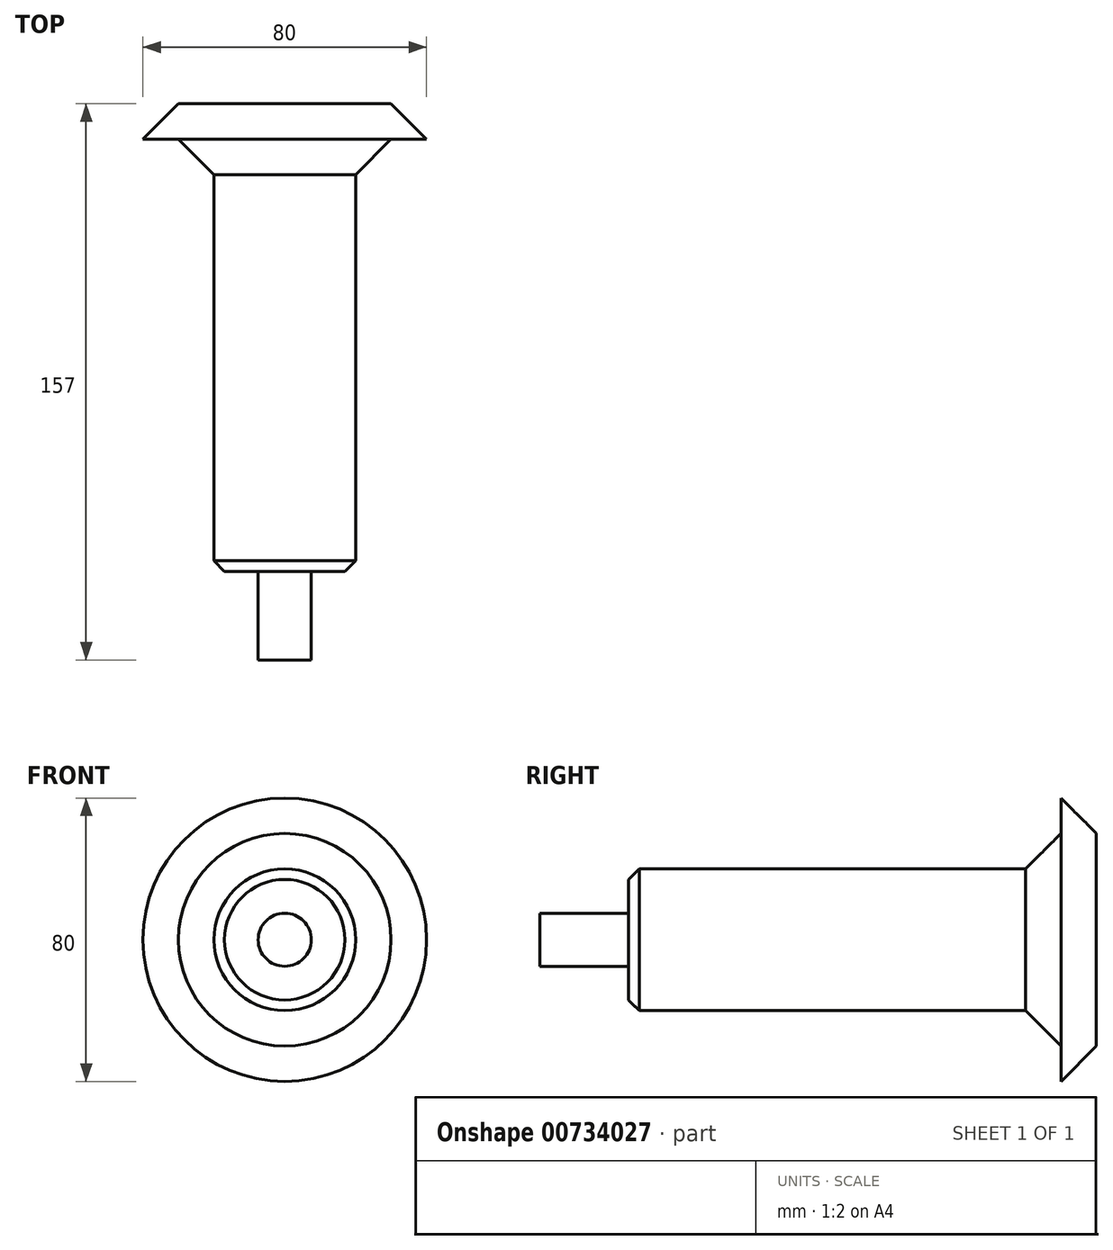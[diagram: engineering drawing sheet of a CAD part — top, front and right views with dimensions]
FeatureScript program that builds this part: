
annotation { "Feature Type Name" : "Feature", "Feature Type Description" : "" }
export const myFeature = defineFeature(function(context is Context, id is Id, definition is map)
    precondition{}
    {
        {
            var Q0;
            Q0=qCreatedBy(makeId("Front.planeOp"),FACE);
            var sketch = newSketch(context, id + "F0", { "sketchPlane" : qUnion([Q0])});
            skCircle(sketch, "E0", {"center": v(0, 0) * mm, "radius": 20 * mm});
            skSolve(sketch);
        }
        {
            var Q0;
            Q0 = qSketchRegion(id + "F0", true);
            extrude(context, id + "F1", {"entities" : qUnion([Q0]), "depth" : 112 * mm, "offsetDistance" : 25.4 * mm});
        }
        {
            var Q0;
            Q0=makeQuery(id+"F1.opExtrude","CAP_EDGE",EDGE,{"disambiguationData":[OSD([sQuery(id+"F0.wireOp",EDGE,"E0")])],"isStart":false});
            chamfer(context, id + "F2", {"entities" : qUnion([Q0]), "width" : 3 * mm, "tangentPropagation" : true});
        }
        {
            var Q0;
            Q0=makeQuery(id+"F1.opExtrude","CAP_FACE",FACE,{"disambiguationData":[OSD([sQuery(id+"F0.wireOp",EDGE,"E0")])],"isStart":false});
            var sketch = newSketch(context, id + "F3", { "sketchPlane" : qUnion([Q0])});
            skCircle(sketch, "E1", {"center": v(0, 0) * mm, "radius": 7.5 * mm});
            skSolve(sketch);
        }
        {
            var Q0;
            Q0 = qSketchRegion(id + "F3", true);
            extrude(context, id + "F4", {"entities" : qUnion([Q0]), "operationType" : NewBodyOperationType.ADD, "depth" : 25 * mm, "offsetDistance" : 25.4 * mm});
        }
        {
            var Q0;
            Q0=makeQuery(id+"F1.opExtrude","CAP_FACE",FACE,{"disambiguationData":[OSD([sQuery(id+"F0.wireOp",EDGE,"E0")])],"isStart":true});
            var sketch = newSketch(context, id + "F5", { "sketchPlane" : qUnion([Q0])});
            skCircle(sketch, "E2", {"center": v(0, 0) * mm, "radius": 30 * mm});
            skSolve(sketch);
        }
        {
            var Q0;
            Q0 = qSketchRegion(id + "F5", true);
            extrude(context, id + "F6", {"entities" : qUnion([Q0]), "operationType" : NewBodyOperationType.ADD, "depth" : 10 * mm, "offsetDistance" : 25.4 * mm});
        }
        {
            var Q0;
            Q0=makeQuery(id+"F6.opExtrude","CAP_EDGE",EDGE,{"disambiguationData":[OSD([sQuery(id+"F5.wireOp",EDGE,"E2")])],"isStart":true});
            chamfer(context, id + "F7", {"entities" : qUnion([Q0]), "width" : 10 * mm, "tangentPropagation" : true});
        }
        {
            var Q0;
            Q0=makeQuery(id+"F6.opExtrude","CAP_FACE",FACE,{"disambiguationData":[OSD([sQuery(id+"F5.wireOp",EDGE,"E2")])],"isStart":false});
            var sketch = newSketch(context, id + "F8", { "sketchPlane" : qUnion([Q0])});
            skCircle(sketch, "E3", {"center": v(0, 0) * mm, "radius": 40 * mm});
            skSolve(sketch);
        }
        {
            var Q0;
            Q0 = qSketchRegion(id + "F8", true);
            extrude(context, id + "F9", {"entities" : qUnion([Q0]), "operationType" : NewBodyOperationType.ADD, "depth" : 10 * mm, "offsetDistance" : 25.4 * mm});
        }
        {
            var Q0;
            Q0=makeQuery(id+"F9.opExtrude","CAP_EDGE",EDGE,{"disambiguationData":[OSD([sQuery(id+"F8.wireOp",EDGE,"E3")])],"isStart":false});
            chamfer(context, id + "F10", {"entities" : qUnion([Q0]), "width" : 10 * mm, "tangentPropagation" : true});
        }
    });
